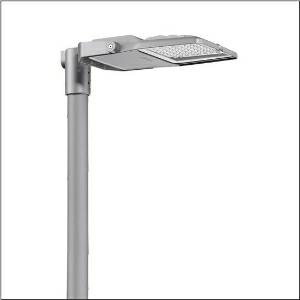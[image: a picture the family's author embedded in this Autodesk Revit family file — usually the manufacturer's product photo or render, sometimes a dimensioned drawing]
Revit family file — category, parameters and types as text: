
# Revit family: floodlight_fl_21_iq_mini___pl33t_5xa7771c4f3a_1d16
name_source: partatom
category: Lighting Fixtures
units: mm (PartAtom-declared; Revit-internal decimal feet)

## family parameters
Cut with Voids When Loaded = No
Host = Face
Light Source = No
Part Type = Normal
Room Calculation Point = No
Round Connector Dimension = Use Diameter
Shared = No

## types (1)
- --- (1 x LED, 12570 lm, 87.2 W, 4000K)
    Apparent Load = 87 VA
    CIE Flux Codes = 26 75 99 100 100
    Color Rendering = 70
    Color Temperature = 4000K
    Default Elevation = 1800 mm
    Description = Floodlight FL 21 iQ mini, floodlight, primary light control with lens, of PMMA, primary optical cover: protective disc, of toughened safety glass, transparent, light distribution: PL33T, light emission: direct distribution, installation type: surface-mounted, lamps: LED, High Power LED, rated values: 12.570lm | 87,2W | 144,2lm/W (begin service life); end service life: 12.570lm | 92,1W; at 50% lumin. flux: 6.285lm | 40,2W | 156,3lm/W, colour temperature: 4000K, colour rendering: CRI > 70, light colour: 740, light setting 1 begin service life: 100% | 12.570lm | 87,2W | 144,2lm/W | 4.000K, light setting 1 end service life: 92,1W, further light settings possible, control: Auto-Match, Temp-Guard, Lumen-Switch, Night-Set, Smart-Wire, Light-Fading, Desk-Remote (wireless, voltage-free reading and setting of iQ features in the workshop via application-optimized NFC function/RFID function), optimised constant luminous flux control (CLO 2.0), pre-setting: linear dimming characteristic, with terminal, 6-pole, mains connection: 220..240V, AC, 50/60Hz, luminaire housing, of diecast aluminium, powder-coated, SITECO metallic grey (DB 702S), corrosivity category C5 mid according to DIN EN ISO 12944suitable for swimming poolschlorine-resistant, sealing non-destructively replaceable, please order mast flange separately, mast bracket, of steel, galvanised, powder-coated, SITECO metallic grey (DB 702S), protection rating (complete): IP66, insulation class (complete): insulation class II (safety insulation), certification: CE, ENEC, VDE, protection symbol: D, impact resistance: IK08, permissible operating ambient temperature: -40..+40°C, permissible operating ambient temperature for outdoor applications: -40..+50°C, standard: DIN EN 12944, LABS conformity tested according to VDMA 24364:2018-05, packaging unit: 1 piece

Light Distribution: PL33T
    Height = 70 mm
    Lamp = 1 x LED
    Lamp Light Flux = 12570 lm
    Lamp Power = 87.2 W
    Lamp count = 1
    Length = 485 mm
    Luminous efficacy = 144 lm/W
    Manufacturer = Siteco
    ModVariant = No
    Model = 5XA7771C4F3A
    Number of Poles = 1
    OnlyDefault = Yes
    Power Factor = 1
    Product Name = Floodlight FL 21 iQ mini | PL33T
    Product group = floodlight | pylon annexe
    ProductGroupID = 6201
    Protection Class = Protection class II
    Protection Degree = IP 66
    RLX_Detail_Level = 1
    RLX_Emergency_Light_Flux = 0 lm
    RLX_Emergency_Type = 0
    RLX_Emergency_Type_DB = No
    RlxData = <blob elided: 101433 chars, md5=6cd70d0f>
    Socket = socket
    Standby Power = 0 W
    System Light Flux = 12570 lm
    System Power = 87 W
    Type Comments = factory setting: luminous flux: 100 % | dim-lin: 254 | 456 mA
    Type Image = l_1007125.jpg
    URL = http://relux.com
    VarID = @adj_149131
    Voltage = 0 V
    Weight = 0.00 kg
    Width = 337 mm

## geometry (parser evidence)
native form markers: Blend x4, Sweep x11
no freeform markers — native parametric forms only
